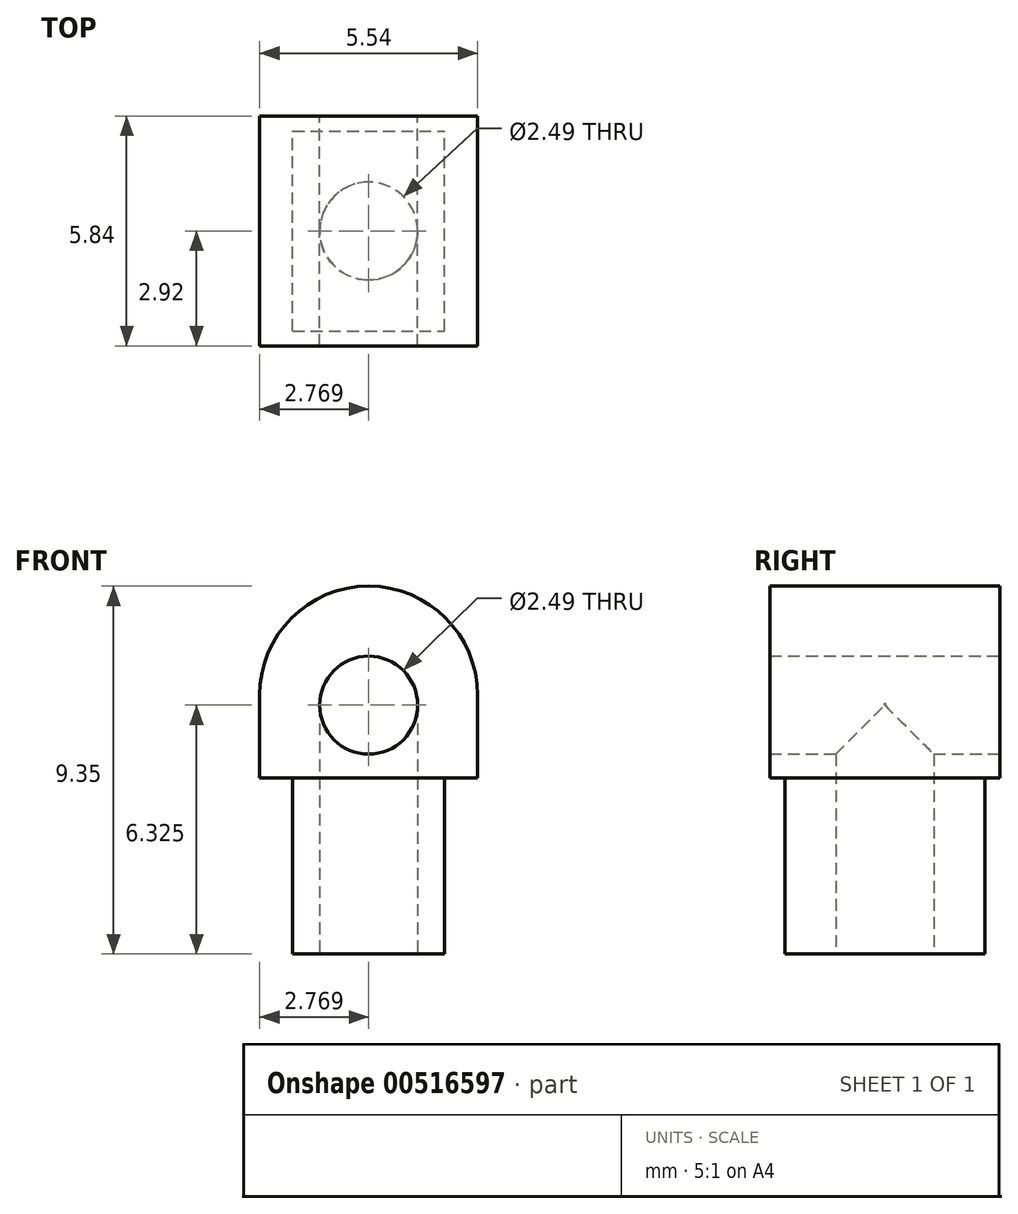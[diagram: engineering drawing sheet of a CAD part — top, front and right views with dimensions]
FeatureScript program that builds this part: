
annotation { "Feature Type Name" : "Feature", "Feature Type Description" : "" }
export const myFeature = defineFeature(function(context is Context, id is Id, definition is map)
    precondition{}
    {
        {
            var Q0;
            Q0=qCreatedBy(makeId("Front.planeOp"),FACE);
            var sketch = newSketch(context, id + "F0", { "sketchPlane" : qUnion([Q0])});
            skLineSegment(sketch, "E0.bottom", {"start": v(0.84, 0) * mm, "end": v(4.7, 0) * mm});
            skLineSegment(sketch, "E0.left", {"start": v(0, 4.47) * mm, "end": v(0, 6.58) * mm});
            skLineSegment(sketch, "E0.right", {"start": v(5.54, 4.47) * mm, "end": v(5.54, 6.58) * mm});
            skLineSegment(sketch, "E1.top", {"start": v(0, 4.47) * mm, "end": v(0.84, 4.47) * mm});
            skLineSegment(sketch, "E1.right", {"start": v(0.84, 0) * mm, "end": v(0.84, 4.47) * mm});
            skLineSegment(sketch, "E2.top", {"start": v(5.54, 4.47) * mm, "end": v(4.7, 4.47) * mm});
            skLineSegment(sketch, "E2.right", {"start": v(4.7, 0) * mm, "end": v(4.7, 4.47) * mm});
            skLineSegment(sketch, "E3", {"start": v(2.77, 0) * mm, "end": v(2.77, 9.35) * mm, "construction": true});
            skLineSegment(sketch, "E4", {"start": v(0, 6.58) * mm, "end": v(5.54, 6.58) * mm, "construction": true});
            skArc(sketch, "E5", {"start": v(5.54, 6.58) * mm, "mid": v(2.77, 9.35) * mm, "end": v(0, 6.58) * mm});
            skPoint(sketch, "E6.orphan", {"position": v(0, 9.35) * mm});
            skCircle(sketch, "E7", {"center": v(2.77, 6.32) * mm, "radius": 1.24 * mm});
            skPoint(sketch, "E8.orphan", {"position": v(5.54, 0) * mm});
            skPoint(sketch, "E9.orphan", {"position": v(0, 0) * mm});
            skLineSegment(sketch, "E10", {"start": v(0.84, 4.47) * mm, "end": v(4.7, 4.47) * mm});
            skSolve(sketch);
        }
        {
            var Q0;
            Q0=makeQuery(id+"F0.imprint","IMPRINT",FACE,{"disambiguationData":[TD([[makeQuery(id+"F0.imprint","IMPRINT",EDGE,{"derivedFrom":sQuery(id+"F0.wireOp",EDGE,"E0.left")}),-1.0]])]});
            extrude(context, id + "F1", {"entities" : qUnion([Q0]), "depth" : 2.92 * mm, "offsetDistance" : 25.4 * mm});
        }
        {
            var Q0;
            Q0=makeQuery(id+"F0.imprint","IMPRINT",FACE,{"disambiguationData":[TD([[makeQuery(id+"F0.imprint","IMPRINT",EDGE,{"derivedFrom":sQuery(id+"F0.wireOp",EDGE,"E0.bottom")}),1.0]])]});
            extrude(context, id + "F2", {"entities" : qUnion([Q0]), "operationType" : NewBodyOperationType.ADD, "depth" : 2.54 * mm, "offsetDistance" : 25.4 * mm});
        }
        {
            var Q0;
            Q0=makeQuery(id+"F0.imprint","IMPRINT",FACE,{"disambiguationData":[TD([[makeQuery(id+"F0.imprint","IMPRINT",EDGE,{"derivedFrom":sQuery(id+"F0.wireOp",EDGE,"E0.left")}),-1.0]])]});
            extrude(context, id + "F3", {"entities" : qUnion([Q0]), "operationType" : NewBodyOperationType.ADD, "oppositeDirection" : true, "depth" : 2.92 * mm, "offsetDistance" : 25.4 * mm});
        }
        {
            var Q0;
            Q0=makeQuery(id+"F0.imprint","IMPRINT",FACE,{"disambiguationData":[TD([[makeQuery(id+"F0.imprint","IMPRINT",EDGE,{"derivedFrom":sQuery(id+"F0.wireOp",EDGE,"E0.bottom")}),1.0]])]});
            extrude(context, id + "F4", {"entities" : qUnion([Q0]), "operationType" : NewBodyOperationType.ADD, "oppositeDirection" : true, "depth" : 2.54 * mm, "offsetDistance" : 25.4 * mm});
        }
        {
            var Q0;
            {var subQ0=sQuery(id+"F0.wireOp",EDGE,"E0.bottom");Q0=makeQuery(id+"F4.boolean.opBoolean","MERGE",FACE,{"derivedFrom":[makeQuery(id+"F2.opExtrude","SWEPT_FACE",FACE,{"disambiguationData":[OSD([subQ0])]}),makeQuery(id+"F4.opExtrude","SWEPT_FACE",FACE,{"disambiguationData":[OSD([subQ0])]})]});}
            var sketch = newSketch(context, id + "F5", { "sketchPlane" : qUnion([Q0])});
            skLineSegment(sketch, "E11", {"start": v(2.77, 2.54) * mm, "end": v(2.77, -2.54) * mm, "construction": true});
            skLineSegment(sketch, "E12", {"start": v(4.7, 0) * mm, "end": v(0.84, 0) * mm, "construction": true});
            skCircle(sketch, "E13", {"center": v(2.77, 0) * mm, "radius": 1.24 * mm});
            skSolve(sketch);
        }
        {
            var Q0;
            Q0 = qSketchRegion(id + "F5", true);
            extrude(context, id + "F6", {"entities" : qUnion([Q0]), "operationType" : NewBodyOperationType.REMOVE, "oppositeDirection" : true, "depth" : 6.35 * mm, "offsetDistance" : 25.4 * mm});
        }
    });
